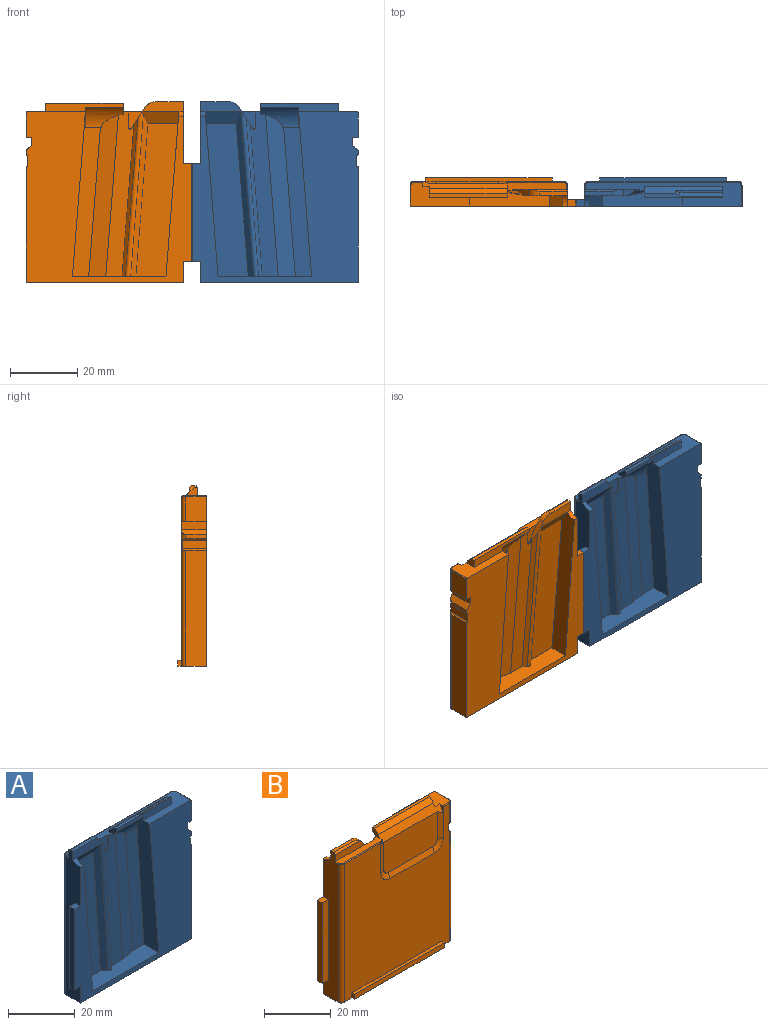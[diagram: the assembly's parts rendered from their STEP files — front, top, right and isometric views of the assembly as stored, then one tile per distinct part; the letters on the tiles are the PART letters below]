
ASSEMBLY  parts=2 mates=1
PART A: 64 faces, bbox 49.8x8.7x54 mm
  f0: plane 46.48x7.18mm, normal (0,0,1), area 140.6mm2, adj f16,f18,f25,f37,f41,f43,f44,f45
  f1: plane 49.07x5.8mm, normal (1,0,0.08), area 259.9mm2, adj f17,f32,f35,f62,f63
  f2: plane 53.85x6.16mm, normal (-1,0,0), area 257.6mm2, adj f6,f13,f14,f17,f27,f36,f37,f38
  f3: plane 6.16x1.27mm, normal (1,0,0), area 7.8mm2, adj f8,f12,f53,f62
  f4: plane 7.37x6.16mm, normal (1,0,0), area 45.4mm2, adj f9,f18,f52,f62
  f5: plane 34.54x6.16mm, normal (1,0,0), area 212.8mm2, adj f6,f11,f53,f62
  f6: plane 46.99x8.57mm, normal (0,0,-1), area 391.7mm2, adj f2,f5,f26,f28,f29,f31,f53,f54
  f7: plane 7.43x2.41mm, normal (1,0,0), area 17.9mm2, adj f8,f9,f26,f62
  f8: plane 7.43x1.52mm, normal (0.71,0,0.71), area 15.5mm2, adj f3,f7,f26,f53,f62
  f9: plane 7.43x1.52mm, normal (0,0,-1), area 11mm2, adj f4,f7,f26,f52,f62
  f10: plane 7.18x2.41mm, normal (1,0,0), area 17.3mm2, adj f11,f12,f53,f62
  f11: cylinder r=0.51mm len=7.18mm, axis (0,-1,0), area 5.6mm2, adj f5,f10,f53,f62
  f12: cylinder r=0.51mm len=7.18mm, axis (0,-1,0), area 5.6mm2, adj f3,f10,f53,f62
  f13: plane 2.54x1.96mm, normal (0,0,-1), area 5mm2, adj f2,f15,f27,f62
  f14: plane 2.54x1.96mm, normal (0,0,1), area 5mm2, adj f2,f15,f27,f62
  f15: plane 29.46x1.96mm, normal (-1,0,0), area 57.6mm2, adj f13,f14,f27,f62
  f16: plane 49.02x6.26mm, normal (-1,0,-0.08), area 291.1mm2, adj f0,f21,f34,f51,f62,f63
  f17: cylinder r=4.34mm len=3.09mm, axis (-1,0,0), area 4.9mm2, adj f1,f2,f38,f62
  f18: cylinder r=0.25mm len=6.16mm, axis (0,1,0), area 2.5mm2, adj f0,f4,f58,f62
  f19: plane 23.24x2.26mm, normal (0,0.67,0.74), area 53.6mm2, adj f20,f46,f47,f50,f60,f61
  f20: plane 23.24x1.02mm, normal (0,0,1), area 15.1mm2, adj f19,f45,f47,f50,f59,f61
  f21: plane 1.4x1.38mm, normal (-1,0,0), area 1mm2, adj f16,f45,f49
  f22: plane 48.33x5.18mm, normal (-0.7,-0.71,-0.07), area 105.7mm2, adj f23,f32,f35,f63
  f23: cylinder r=1.02mm len=49.01mm, axis (-0.08,-0.01,1), area 77.2mm2, adj f22,f24,f35,f43,f63
  f24: plane 47.22x4.8mm, normal (0.7,-0.71,0.05), area 70.8mm2, adj f23,f25,f43,f63
  f25: plane 49.03x8.42mm, normal (0,-1,-0.01), area 227.4mm2, adj f0,f24,f33,f40,f41,f43,f49,f50
  f26: plane 50.55x44.45mm, normal (0,1,0), area 2178.8mm2, adj f6,f7,f8,f9,f28,f29,f30,f52
  f27: plane 29.46x2.54mm, normal (0,1,0), area 74.8mm2, adj f2,f13,f14,f15
  f28: plane 1.78x1.14mm, normal (1,0,0), area 2mm2, adj f6,f26,f30,f31
  f29: plane 1.78x1.14mm, normal (-1,0,0), area 2mm2, adj f6,f26,f30,f31
  f30: plane 37.85x1.14mm, normal (0,0,1), area 43.3mm2, adj f26,f28,f29,f31
  f31: plane 37.85x1.78mm, normal (0,1,0), area 67.3mm2, adj f6,f28,f29,f30
  f32: plane 45.57x12.59mm, normal (0,-1,-0.01), area 410.5mm2, adj f1,f22,f35,f63
  f33: plane 49.02x8.89mm, normal (0.2,-0.98,0), area 243.9mm2, adj f25,f34,f48,f49,f63
  f34: plane 49.02x8.7mm, normal (0,-1,-0.01), area 237.3mm2, adj f16,f33,f48,f63
  f35: plane 11.28x3.59mm, normal (0,-0.86,-0.51), area 40.1mm2, adj f1,f22,f23,f32,f38,f43
  f36: cylinder r=0.64mm len=10.44mm, axis (-1,0,0), area 9.4mm2, adj f2,f37,f39,f42
  f37: plane 12.38x2.67mm, normal (0,1,0), area 27.9mm2, adj f0,f2,f36,f42,f43,f55
  f38: plane 12.38x3.05mm, normal (0,-1,0), area 34.1mm2, adj f2,f17,f35,f39,f42,f43
  f39: plane 8.33x1.17mm, normal (0,0,1), area 9.8mm2, adj f2,f36,f38,f42
  f40: cylinder r=0.51mm len=0.93mm, axis (0,1,0), area 0.5mm2, adj f25,f41,f43,f44
  f41: plane 4.64x0.47mm, normal (-1,0,0), area 2mm2, adj f0,f25,f40,f44
  f42: cylinder r=3.81mm len=3.19mm, axis (0,1,0), area 6.1mm2, adj f36,f37,f38,f39,f43
  f43: plane 6.36x4.18mm, normal (0.84,0,0.54), area 9.4mm2, adj f0,f23,f24,f25,f35,f37,f38,f40
  f44: plane 5.14x4.13mm, normal (0,-1,0), area 12.6mm2, adj f0,f40,f41,f43
  f45: plane 23.24x2.54mm, normal (0,-1,0), area 43.2mm2, adj f0,f20,f21,f47,f49,f50
  f46: plane 23.24x0.49mm, normal (0,1,0), area 11.3mm2, adj f0,f19,f47,f50
  f47: plane 3.28x2.54mm, normal (1,0,0), area 5.5mm2, adj f0,f19,f20,f45,f46,f59,f60
  f48: plane 4.84x4.7mm, normal (0,1,0), area 22.7mm2, adj f33,f34,f49,f51
  f49: cylinder r=7.75mm len=11.3mm, axis (1,0,0), area 60.2mm2, adj f21,f25,f33,f45,f48,f50,f51
  f50: plane 3.42x3.28mm, normal (-1,0,0), area 5.2mm2, adj f0,f19,f20,f25,f45,f46,f49
  f51: plane 4.7x1.59mm, normal (1,0,0), area 2.4mm2, adj f16,f48,f49
  f52: cylinder r=1.27mm len=7.37mm, axis (0,0,1), area 14.7mm2, adj f4,f9,f26,f58
  f53: cylinder r=1.27mm len=40.51mm, axis (0,0,1), area 75.3mm2, adj f3,f5,f6,f8,f10,f11,f12,f26
  f54: cylinder r=1.27mm len=50.55mm, axis (0,0,-1), area 100.8mm2, adj f2,f6,f26,f56
  f55: cylinder r=0.25mm len=1.27mm, axis (0,-1,0), area 0.5mm2, adj f0,f2,f37,f56
  f56: torus R=1.02mm, axis (0,0,1), area 0.7mm2, adj f0,f54,f55,f57
  f57: cylinder r=0.25mm len=44.45mm, axis (-1,0,0), area 17.7mm2, adj f0,f26,f56,f58
  f58: torus R=1.02mm, axis (0,0,1), area 0.7mm2, adj f0,f18,f52,f57
  f59: plane 12.73x0.92mm, normal (0,0.67,0.74), area 15.8mm2, adj f20,f47,f60,f61
  f60: plane 13.97x0.64mm, normal (0,0,1), area 8.5mm2, adj f19,f47,f59,f61
  f61: plane 1.56x1.24mm, normal (0.33,0.64,0.7), area 1.6mm2, adj f19,f20,f59,f60
  f62: plane 50.8x49.53mm, normal (0,-1,0), area 1085.9mm2, adj f0,f1,f2,f3,f4,f5,f6,f7
  f63: plane 27.91x6.27mm, normal (0,0,1), area 155.5mm2, adj f1,f16,f22,f23,f24,f25,f32,f33
PART B: 75 faces, bbox 49.8x8.7x54 mm
  f0: plane 49.02x8.89mm, normal (0.2,0.98,0), area 243.9mm2, adj f1,f6,f30,f31,f74
  f1: plane 49.03x8.42mm, normal (0,1,-0.01), area 227.4mm2, adj f0,f2,f20,f21,f22,f23,f30,f32
  f2: plane 47.22x4.8mm, normal (0.7,0.71,0.05), area 70.8mm2, adj f1,f3,f32,f74
  f3: cylinder r=1.02mm len=49.01mm, axis (-0.08,0.01,1), area 77.2mm2, adj f2,f4,f32,f39,f74
  f4: plane 48.33x5.18mm, normal (-0.7,0.71,-0.07), area 105.7mm2, adj f3,f5,f39,f74
  f5: plane 45.57x12.59mm, normal (0,1,-0.01), area 410.5mm2, adj f4,f8,f39,f74
  f6: plane 49.02x8.7mm, normal (0,1,-0.01), area 237.3mm2, adj f0,f7,f31,f74
  f7: plane 49.02x6.26mm, normal (-1,0,-0.08), area 291.1mm2, adj f6,f52,f53,f72,f73,f74
  f8: plane 49.07x5.8mm, normal (1,0,0.08), area 259.9mm2, adj f5,f39,f59,f73,f74
  f9: cone r=1.91mm half-angle=70deg, axis (0,-1,0), area 9.1mm2, adj f10,f13,f16,f24
  f10: plane 18.75x1.91mm, normal (0,-0.94,0.34), area 38mm2, adj f9,f11,f16,f25
  f11: cone r=1.91mm half-angle=70deg, axis (0,-1,0), area 9.1mm2, adj f10,f15,f16,f26
  f12: plane 5.14x4.13mm, normal (0,1,0), area 12.6mm2, adj f20,f21,f22,f32
  f13: plane 11.43x1.91mm, normal (0.34,-0.94,0), area 21.9mm2, adj f9,f14,f16,f20,f28,f29,f36
  f14: plane 1.83x1.11mm, normal (1,0,0), area 1mm2, adj f13,f20,f36
  f15: plane 10.04x1.91mm, normal (-0.34,-0.94,0), area 19.2mm2, adj f11,f16,f35,f36
  f16: plane 22.56x11.94mm, normal (0,-1,0), area 267.9mm2, adj f9,f10,f11,f13,f15,f36
  f17: plane 23.24x1.59mm, normal (0,-0.67,0.74), area 50mm2, adj f18,f23,f36,f37
  f18: plane 23.24x1.02mm, normal (0,0,1), area 23.6mm2, adj f17,f23,f37,f38
  f19: torus R=1.02mm, axis (0,0,1), area 0.7mm2, adj f20,f28,f43,f44
  f20: plane 17.72x2.61mm, normal (0,0,1), area 39.9mm2, adj f1,f12,f13,f14,f19,f21,f23,f28
  f21: plane 4.64x0.47mm, normal (-1,0,0), area 2mm2, adj f1,f12,f20,f22
  f22: cylinder r=0.51mm len=0.93mm, axis (0,1,0), area 0.5mm2, adj f1,f12,f21,f32
  f23: plane 3.42x3.27mm, normal (-1,0,0), area 5mm2, adj f1,f17,f18,f20,f30,f36,f38
  f24: cylinder r=3.81mm len=3.81mm, axis (0,-1,0), area 0mm2, adj f9,f25,f29,f48
  f25: plane 18.75x0.01mm, normal (0,0,1), area 0.1mm2, adj f10,f24,f26,f48
  f26: cylinder r=3.81mm len=3.81mm, axis (0,-1,0), area 0mm2, adj f11,f25,f35,f48
  f27: plane 37.85x1.14mm, normal (0,0,1), area 43.3mm2, adj f45,f46,f47,f48
  f28: cylinder r=0.25mm len=16.22mm, axis (1,0,0), area 6.3mm2, adj f13,f19,f20,f29,f48
  f29: plane 11.23x0.01mm, normal (1,0,0), area 0.1mm2, adj f13,f24,f28,f48
  f30: cylinder r=7.75mm len=11.3mm, axis (1,0,0), area 60.2mm2, adj f0,f1,f23,f31,f38,f52,f53
  f31: plane 4.84x4.7mm, normal (0,-1,0), area 22.7mm2, adj f0,f6,f30,f53
  f32: plane 6.36x4.18mm, normal (0.84,0,0.54), area 9.5mm2, adj f1,f2,f3,f12,f20,f22,f33,f39
  f33: cylinder r=3.81mm len=3.19mm, axis (0,1,0), area 6.2mm2, adj f32,f40,f41,f42,f54
  f34: cylinder r=0.25mm len=2.54mm, axis (1,0,0), area 1mm2, adj f35,f48,f55,f72
  f35: plane 11.43x1.54mm, normal (-1,0,0), area 2mm2, adj f15,f26,f34,f36,f48,f72
  f36: plane 25.21x3.62mm, normal (0,-0.85,0.52), area 72.2mm2, adj f13,f14,f15,f16,f17,f23,f35,f37
  f37: plane 3.27x2.54mm, normal (1,0,0), area 5.8mm2, adj f17,f18,f36,f38,f72
  f38: plane 23.24x2.54mm, normal (0,1,0), area 43.2mm2, adj f18,f23,f30,f37,f52,f72
  f39: plane 11.28x3.59mm, normal (0,0.86,-0.51), area 40.1mm2, adj f3,f4,f5,f8,f32,f54
  f40: plane 8.33x1.19mm, normal (0,0,1), area 9.9mm2, adj f33,f41,f54,f71
  f41: cylinder r=0.64mm len=10.44mm, axis (-1,0,0), area 9.4mm2, adj f33,f40,f42,f71
  f42: plane 12.38x2.67mm, normal (0,-1,0), area 27.9mm2, adj f20,f32,f33,f41,f43,f71
  f43: cylinder r=0.25mm len=1.25mm, axis (0,-1,0), area 0.5mm2, adj f19,f20,f42,f71
  f44: cylinder r=1.27mm len=50.55mm, axis (0,0,1), area 100.8mm2, adj f19,f48,f68,f71
  f45: plane 1.78x1.14mm, normal (-1,0,0), area 2mm2, adj f27,f46,f48,f68
  f46: plane 37.85x1.78mm, normal (0,-1,0), area 67.3mm2, adj f27,f45,f47,f68
  f47: plane 1.78x1.14mm, normal (1,0,0), area 2mm2, adj f27,f46,f48,f68
  f48: plane 50.55x44.45mm, normal (0,-1,0), area 1789.9mm2, adj f24,f25,f26,f27,f28,f29,f34,f35
  f49: cylinder r=1.27mm len=7.37mm, axis (0,0,-1), area 14.7mm2, adj f48,f55,f61,f64
  f50: cylinder r=1.27mm len=40.51mm, axis (0,0,-1), area 75.3mm2, adj f48,f62,f65,f66,f67,f68,f69,f70
  f51: plane 29.46x2.54mm, normal (0,-1,0), area 74.8mm2, adj f56,f57,f58,f71
  f52: plane 1.4x1.38mm, normal (-1,0,0), area 1mm2, adj f7,f30,f38
  f53: plane 4.7x1.59mm, normal (1,0,0), area 2.4mm2, adj f7,f30,f31
  f54: plane 12.38x3.05mm, normal (0,1,0), area 34.1mm2, adj f32,f33,f39,f40,f59,f71
  f55: torus R=1.02mm, axis (0,0,1), area 0.7mm2, adj f34,f49,f60,f72
  f56: plane 29.46x1.96mm, normal (-1,0,0), area 57.6mm2, adj f51,f57,f58,f73
  f57: plane 2.54x1.96mm, normal (0,0,1), area 5mm2, adj f51,f56,f71,f73
  f58: plane 2.54x1.96mm, normal (0,0,-1), area 5mm2, adj f51,f56,f71,f73
  f59: cylinder r=4.34mm len=3.09mm, axis (-1,0,0), area 4.9mm2, adj f8,f54,f71,f73
  f60: cylinder r=0.25mm len=6.16mm, axis (0,1,0), area 2.5mm2, adj f55,f64,f72,f73
  f61: plane 7.43x1.52mm, normal (0,0,-1), area 11mm2, adj f48,f49,f63,f64,f73
  f62: plane 7.43x1.52mm, normal (0.71,0,0.71), area 15.5mm2, adj f48,f50,f63,f70,f73
  f63: plane 7.43x2.41mm, normal (1,0,0), area 17.9mm2, adj f48,f61,f62,f73
  f64: plane 7.37x6.16mm, normal (1,0,0), area 45.4mm2, adj f49,f60,f61,f73
  f65: cylinder r=0.51mm len=7.18mm, axis (0,-1,0), area 5.6mm2, adj f50,f67,f70,f73
  f66: cylinder r=0.51mm len=7.18mm, axis (0,-1,0), area 5.6mm2, adj f50,f67,f69,f73
  f67: plane 7.18x2.41mm, normal (1,0,0), area 17.3mm2, adj f50,f65,f66,f73
  f68: plane 46.99x8.57mm, normal (0,0,-1), area 391.7mm2, adj f44,f45,f46,f47,f48,f50,f69,f71
  f69: plane 34.54x6.16mm, normal (1,0,0), area 212.8mm2, adj f50,f66,f68,f73
  f70: plane 6.16x1.27mm, normal (1,0,0), area 7.8mm2, adj f50,f62,f65,f73
  f71: plane 53.85x6.16mm, normal (-1,0,0), area 257.7mm2, adj f40,f41,f42,f43,f44,f51,f54,f57
  f72: plane 17.46x7.18mm, normal (0,0,1), area 68.1mm2, adj f7,f34,f35,f36,f37,f38,f55,f60
  f73: plane 50.8x49.53mm, normal (0,1,0), area 1085.9mm2, adj f7,f8,f56,f57,f58,f59,f60,f61
  f74: plane 27.91x6.27mm, normal (0,0,1), area 155.5mm2, adj f0,f1,f2,f3,f4,f5,f6,f7
PLACE A t=(62.61,-4.29,5.05)mm
PLACE B rot(axis=(0,0,1),180deg) t=(10.54,-4.29,5.05)mm fixed
MATE planar B.f56 <-> A.f15  axis (1,0,0) through (36.58,-3.31,-24.92)mm
